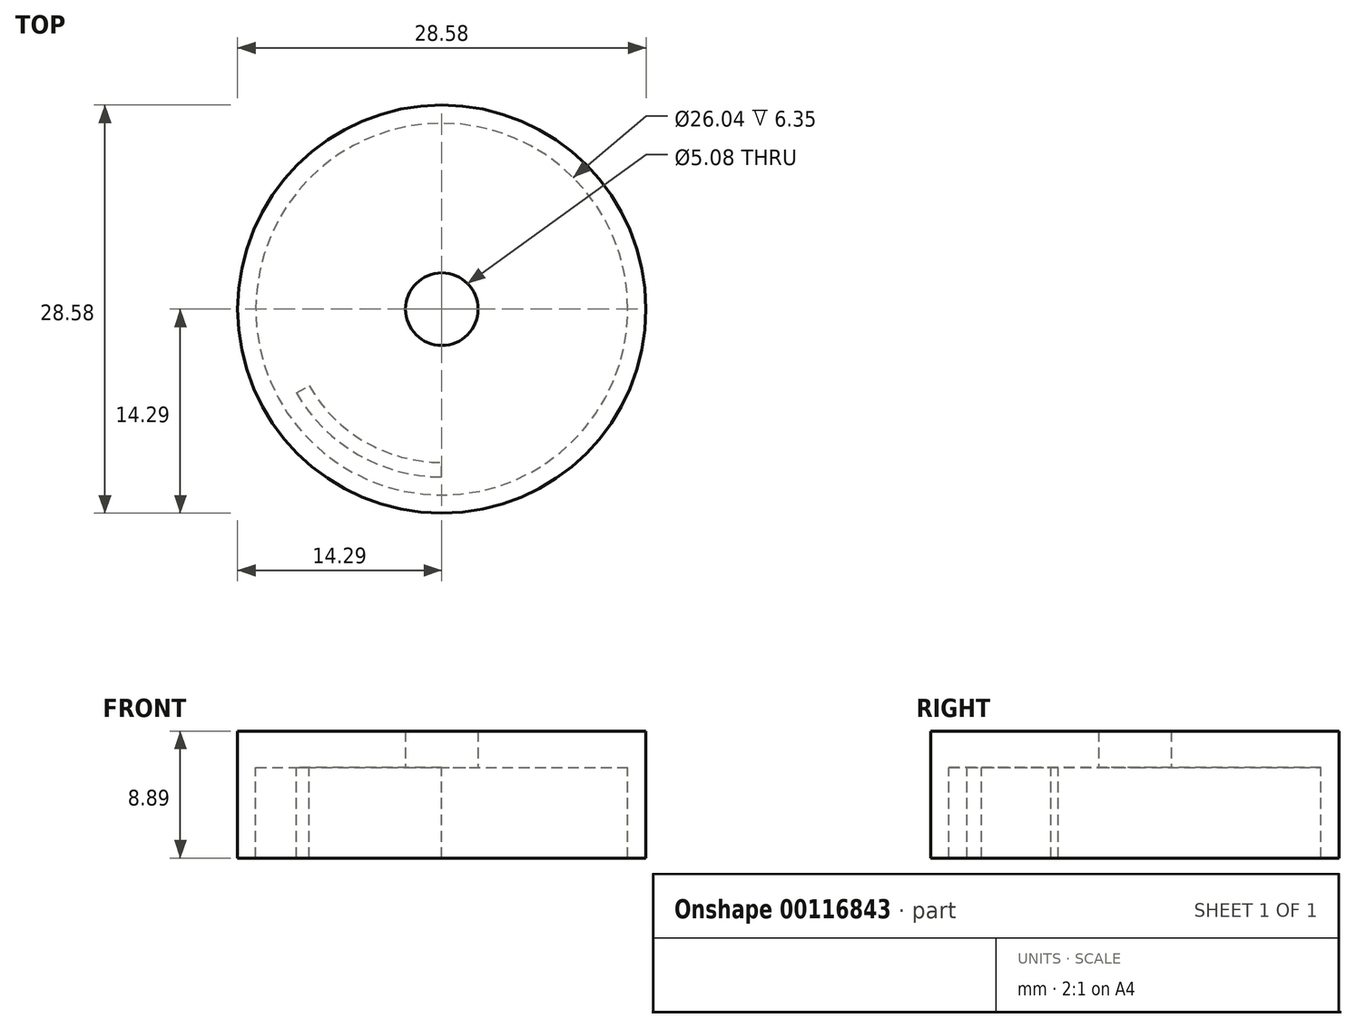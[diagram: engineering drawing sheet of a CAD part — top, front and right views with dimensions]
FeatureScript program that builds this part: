
annotation { "Feature Type Name" : "Feature", "Feature Type Description" : "" }
export const myFeature = defineFeature(function(context is Context, id is Id, definition is map)
    precondition{}
    {
        {
            var Q0;
            Q0=qCreatedBy(makeId("Top.planeOp"),FACE);
            var sketch = newSketch(context, id + "F0", { "sketchPlane" : qUnion([Q0])});
            skCircle(sketch, "E0", {"center": v(0, 0) * mm, "radius": 14.29 * mm});
            skSolve(sketch);
        }
        {
            var Q0;
            Q0 = qSketchRegion(id + "F0", true);
            extrude(context, id + "F1", {"entities" : qUnion([Q0]), "depth" : 2.54 * mm});
        }
        {
            var Q0;
            Q0=makeQuery(id+"F1.opExtrude","CAP_FACE",FACE,{"disambiguationData":[OSD([sQuery(id+"F0.wireOp",EDGE,"E0")])],"isStart":true});
            var sketch = newSketch(context, id + "F2", { "sketchPlane" : qUnion([Q0])});
            skCircle(sketch, "E1.0", {"center": v(0, 0) * mm, "radius": 14.29 * mm});
            skCircle(sketch, "E2.0", {"center": v(0, 0) * mm, "radius": 13.02 * mm});
            skLineSegment(sketch, "E3", {"start": v(0, 13.02) * mm, "end": v(0, 0) * mm, "construction": true});
            skLineSegment(sketch, "E4", {"start": v(-11.27, 6.5) * mm, "end": v(0, 0) * mm, "construction": true});
            skArc(sketch, "E5.0", {"start": v(0, 11.75) * mm, "mid": v(-5.87, 10.17) * mm, "end": v(-10.17, 5.87) * mm});
            skArc(sketch, "E6.0", {"start": v(0, 10.73) * mm, "mid": v(-5.37, 9.3) * mm, "end": v(-9.3, 5.37) * mm});
            skLineSegment(sketch, "E7", {"start": v(0, 11.75) * mm, "end": v(0, 10.73) * mm});
            skLineSegment(sketch, "E8", {"start": v(-10.17, 5.87) * mm, "end": v(-9.3, 5.37) * mm});
            skSolve(sketch);
        }
        {
            var Q0;
            Q0 = qSketchRegion(id + "F2", true);
            extrude(context, id + "F3", {"entities" : qUnion([Q0]), "operationType" : NewBodyOperationType.ADD, "depth" : 6.35 * mm});
        }
        {
            var Q0;
            Q0=makeQuery(id+"F2.imprint","IMPRINT",FACE,{"disambiguationData":[TD([[makeQuery(id+"F2.imprint","IMPRINT",EDGE,{"derivedFrom":sQuery(id+"F2.wireOp",EDGE,"E5.0")}),1.0]])]});
            var Q1;
            Q1=makeQuery(id+"F3.opExtrude","CAP_FACE",FACE,{"disambiguationData":[OSD([sQuery(id+"F2.wireOp",EDGE,"E1.0"),sQuery(id+"F2.wireOp",EDGE,"E2.0")])],"isStart":false});
            extrude(context, id + "F4", {"entities" : qUnion([Q0]), "operationType" : NewBodyOperationType.ADD, "endBound" : BoundingType.UP_TO_SURFACE, "endBoundEntityFace" : qUnion([Q1]), "depth" : 25.4 * mm});
        }
        {
            var Q0;
            Q0=makeQuery(id+"F2.imprint","IMPRINT",FACE,{"disambiguationData":[TD([[makeQuery(id+"F2.imprint","IMPRINT",EDGE,{"derivedFrom":sQuery(id+"F2.wireOp",EDGE,"E2.0")}),1.0]])]});
            var sketch = newSketch(context, id + "F5", { "sketchPlane" : qUnion([Q0])});
            skCircle(sketch, "E9", {"center": v(0, 0) * mm, "radius": 2.54 * mm});
            skSolve(sketch);
        }
        {
            var Q0;
            Q0 = qSketchRegion(id + "F5", true);
            extrude(context, id + "F6", {"entities" : qUnion([Q0]), "operationType" : NewBodyOperationType.REMOVE, "oppositeDirection" : true, "depth" : 25.4 * mm});
        }
    });
